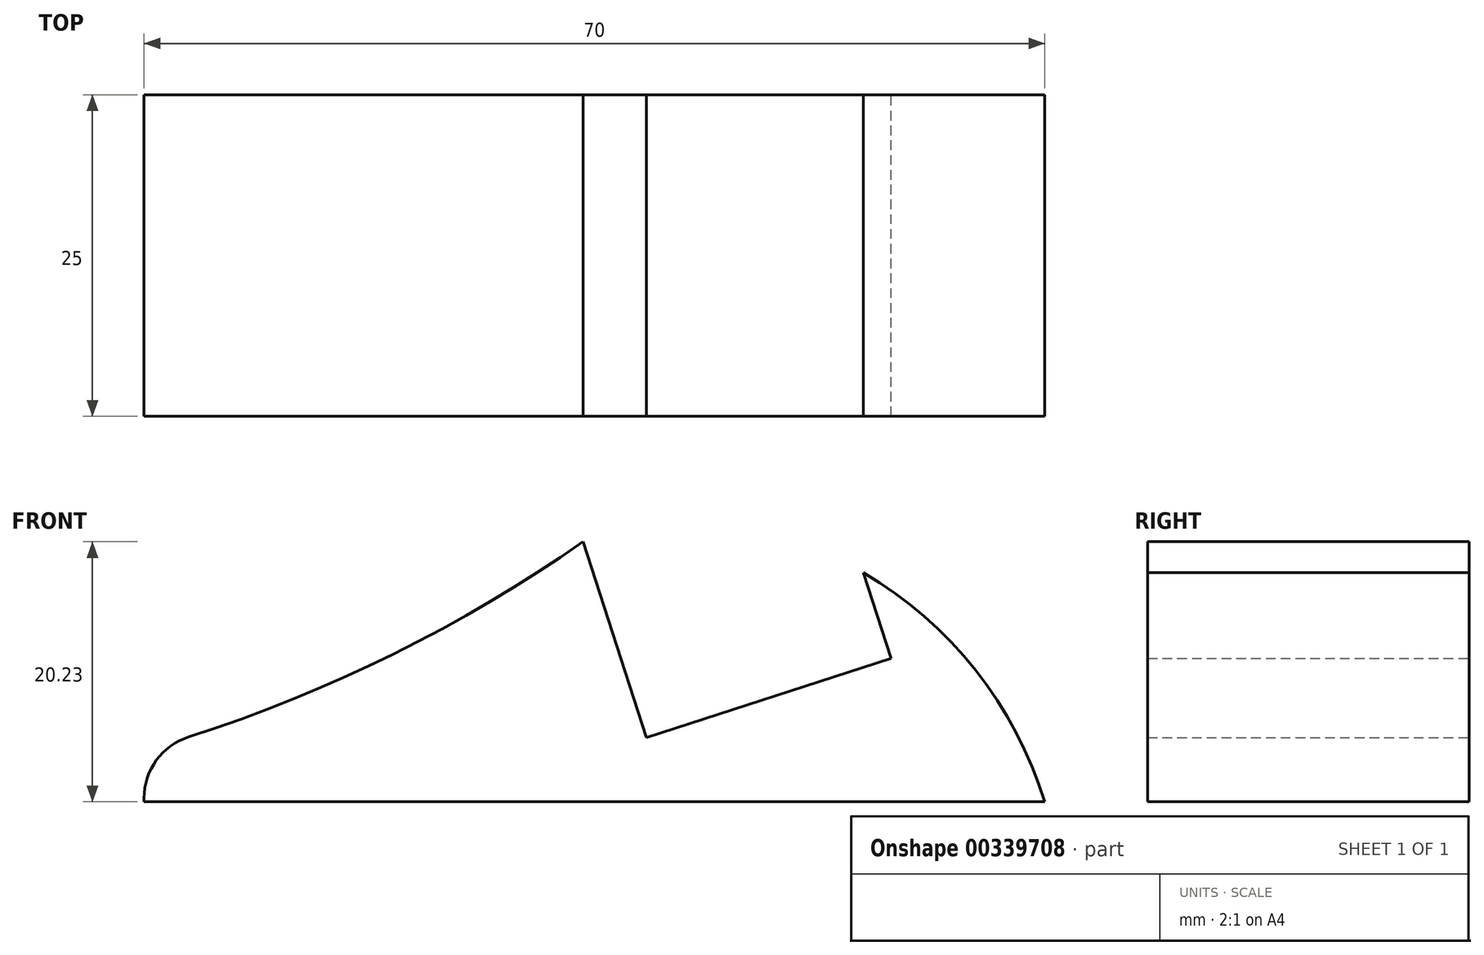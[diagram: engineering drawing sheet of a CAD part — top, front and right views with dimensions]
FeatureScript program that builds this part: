
annotation { "Feature Type Name" : "Feature", "Feature Type Description" : "" }
export const myFeature = defineFeature(function(context is Context, id is Id, definition is map)
    precondition{}
    {
        {
            var Q0;
            Q0=qCreatedBy(makeId("Front.planeOp"),FACE);
            var sketch = newSketch(context, id + "F0", { "sketchPlane" : qUnion([Q0])});
            skLineSegment(sketch, "E0", {"start": v(-26.66, 0) * mm, "end": v(43.34, 0) * mm});
            skLineSegment(sketch, "E1", {"start": v(12.38, 5) * mm, "end": v(7.46, 20.23) * mm});
            skLineSegment(sketch, "E2", {"start": v(12.38, 5) * mm, "end": v(31.4, 11.15) * mm});
            skLineSegment(sketch, "E3", {"start": v(31.4, 11.15) * mm, "end": v(29.26, 17.8) * mm});
            skArc(sketch, "E4", {"start": v(43.34, 0) * mm, "mid": v(37.98, 10.24) * mm, "end": v(29.26, 17.8) * mm});
            skLineSegment(sketch, "E5", {"start": v(-26.66, 0) * mm, "end": v(-26.66, 4) * mm});
            skArc(sketch, "E6", {"start": v(-26.66, 4) * mm, "mid": v(-8.93, 10.69) * mm, "end": v(7.46, 20.23) * mm});
            skSolve(sketch);
        }
        {
            var Q0;
            Q0 = qSketchRegion(id + "F0", true);
            extrude(context, id + "F1", {"entities" : qUnion([Q0]), "depth" : 25 * mm});
        }
        {
            var Q0;
            Q0=makeQuery(id+"F1.opExtrude","SWEPT_EDGE",EDGE,{"disambiguationData":[OSD([sQuery(id+"F0.wireOp",EDGE,"E5"),sQuery(id+"F0.wireOp",EDGE,"E6")])]});
            fillet(context, id + "F2", {"entities" : qUnion([Q0]), "radius" : 5 * mm, "tangentPropagation" : true, "allowEdgeOverflow" : false});
        }
    });
